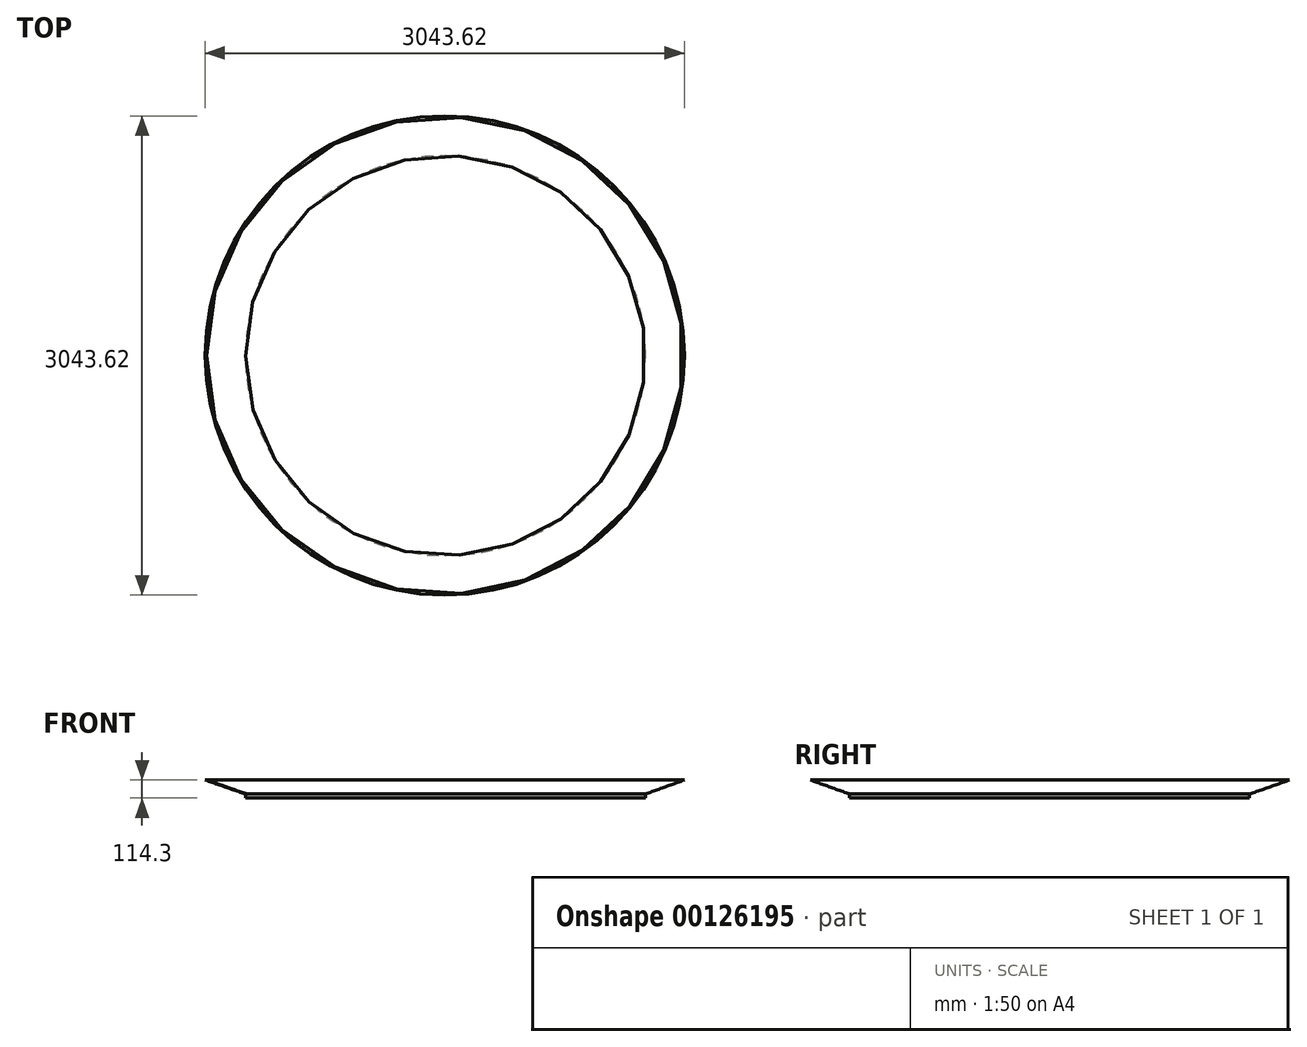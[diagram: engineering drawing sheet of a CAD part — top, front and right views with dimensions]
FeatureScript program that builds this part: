
annotation { "Feature Type Name" : "Feature", "Feature Type Description" : "" }
export const myFeature = defineFeature(function(context is Context, id is Id, definition is map)
    precondition{}
    {
        {
            var Q0;
            Q0=qCreatedBy(makeId("Top.planeOp"),FACE);
            var sketch = newSketch(context, id + "F0", { "sketchPlane" : qUnion([Q0])});
            skCircle(sketch, "E0", {"center": v(-803.18, 913.77) * mm, "radius": 1270 * mm});
            skSolve(sketch);
        }
        {
            var Q0;
            Q0=makeQuery(id+"F0.imprint","IMPRINT",FACE,{"disambiguationData":[TD([[makeQuery(id+"F0.imprint","IMPRINT",EDGE,{"derivedFrom":sQuery(id+"F0.wireOp",EDGE,"E0")}),1.0]])]});
            cPlane(context, id + "F1", {"entities" : qUnion([Q0]), "cplaneType" : CPlaneType.OFFSET, "offset" : 114.3 * mm, "width" : 152.4 * mm, "height" : 152.4 * mm});
        }
        {
            var Q0;
            Q0=qCreatedBy(id+"F1.planeOp",FACE);
            var sketch = newSketch(context, id + "F2", { "sketchPlane" : qUnion([Q0])});
            skCircle(sketch, "E1", {"center": v(-807.36, 915.47) * mm, "radius": 1521.8 * mm});
            skSolve(sketch);
        }
        {
            var Q0;
            Q0 = qSketchRegion(id + "F0", true);
            extrude(context, id + "F3", {"entities" : qUnion([Q0]), "depth" : 25.4 * mm});
        }
        {
            var Q0;
            Q0=makeQuery(id+"F2.imprint","IMPRINT",FACE,{"disambiguationData":[TD([[makeQuery(id+"F2.imprint","IMPRINT",EDGE,{"derivedFrom":sQuery(id+"F2.wireOp",EDGE,"E1")}),1.0]])]});
            var Q1;
            Q1=makeQuery(id+"F3.opExtrude","CAP_FACE",FACE,{"disambiguationData":[OSD([sQuery(id+"F0.wireOp",EDGE,"E0")])],"isStart":false});
            loft(context, id + "F4", {"sheetProfilesArray" : [{ "sheetProfileEntities" : qUnion([Q0]) }, { "sheetProfileEntities" : qUnion([Q1]) }]});
        }
        {
            var Q0;
            Q0=makeQuery(id+"F4.opLoft","CAP_FACE",FACE,{"disambiguationData":[OSD([makeQuery(id+"F2.imprint","IMPRINT",FACE,{"disambiguationData":[TD([[makeQuery(id+"F2.imprint","IMPRINT",EDGE,{"derivedFrom":sQuery(id+"F2.wireOp",EDGE,"E1")}),1.0]])]})])],"isStart":true});
            shell(context, id + "F5", {"entities" : qUnion([Q0]), "thickness" : 2.54 * mm});
        }
    });
